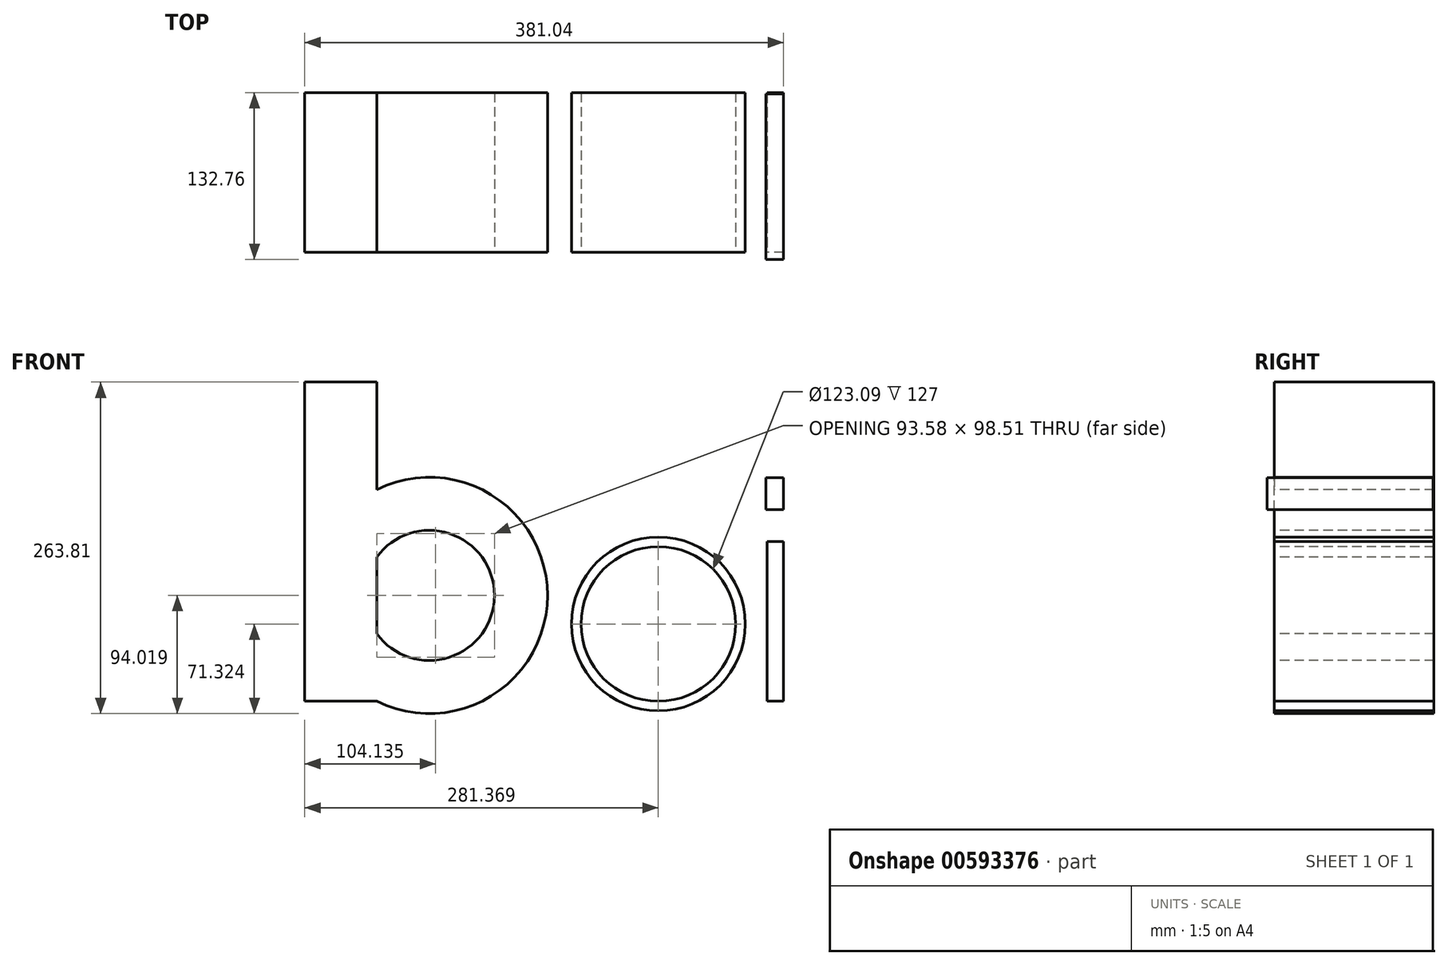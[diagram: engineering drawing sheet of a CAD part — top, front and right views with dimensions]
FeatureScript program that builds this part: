
annotation { "Feature Type Name" : "Feature", "Feature Type Description" : "" }
export const myFeature = defineFeature(function(context is Context, id is Id, definition is map)
    precondition{}
    {
        {
            var Q0;
            Q0=qCreatedBy(makeId("Top.planeOp"),FACE);
            var sketch = newSketch(context, id + "F0", { "sketchPlane" : qUnion([Q0])});
            skLineSegment(sketch, "E0.bottom", {"start": v(190.5, 63.5) * mm, "end": v(-190.5, 63.5) * mm});
            skLineSegment(sketch, "E0.top", {"start": v(190.5, -63.5) * mm, "end": v(-190.5, -63.5) * mm});
            skLineSegment(sketch, "E0.left", {"start": v(190.5, 63.5) * mm, "end": v(190.5, -63.5) * mm});
            skLineSegment(sketch, "E0.right", {"start": v(-190.5, 63.5) * mm, "end": v(-190.5, -63.5) * mm});
            skPoint(sketch, "E0.middle", {"position": v(0, 0) * mm});
            skLineSegment(sketch, "E1", {"start": v(-133.15, -63.5) * mm, "end": v(-133.15, 63.5) * mm});
            skLineSegment(sketch, "E2", {"start": v(-38.93, 63.5) * mm, "end": v(-38.93, -63.5) * mm});
            skLineSegment(sketch, "E3", {"start": v(59.74, 63.5) * mm, "end": v(59.74, -63.5) * mm});
            skLineSegment(sketch, "E4", {"start": v(59.74, -63.5) * mm, "end": v(122.52, -63.5) * mm});
            skLineSegment(sketch, "E5", {"start": v(122.52, 63.5) * mm, "end": v(122.52, -63.5) * mm});
            skLineSegment(sketch, "E6", {"start": v(88.9, 63.5) * mm, "end": v(88.9, -63.5) * mm});
            skLineSegment(sketch, "E7", {"start": v(177.27, 63.5) * mm, "end": v(177.27, -63.5) * mm});
            skSolve(sketch);
        }
        {
            var Q0;
            {var subQ0=sQuery(id+"F0.wireOp",EDGE,"E0.right");Q0=makeQuery(id+"F0.imprint","IMPRINT",FACE,{"disambiguationData":[TD([[makeQuery(id+"F0.imprint","IMPRINT",EDGE,{"derivedFrom":subQ0}),1.0]])]});}
            extrude(context, id + "F1", {"entities" : qUnion([Q0]), "depth" : 254 * mm, "offsetDistance" : 25.4 * mm});
        }
        {
            var Q0;
            Q0=qCreatedBy(makeId("Front.planeOp"),FACE);
            var sketch = newSketch(context, id + "F2", { "sketchPlane" : qUnion([Q0])});
            skCircle(sketch, "E8", {"center": v(-91.34, 84.2) * mm, "radius": 37.73 * mm});
            skSolve(sketch);
        }
        {
            var Q0;
            Q0=makeQuery(id+"F1.opExtrude","SWEPT_FACE",FACE,{"disambiguationData":[OSD([sQuery(id+"F0.wireOp",EDGE,"E1")])]});
            var sketch = newSketch(context, id + "F3", { "sketchPlane" : qUnion([Q0])});
            skLineSegment(sketch, "E9", {"start": v(-63.5, 53.7) * mm, "end": v(63.5, 53.7) * mm});
            skSolve(sketch);
        }
        {
            var Q0;
            {var subQ0=sQuery(id+"F3.wireOp",EDGE,"E9");Q0=makeQuery(id+"F3.imprint","IMPRINT",FACE,{"disambiguationData":[TD([[makeQuery(id+"F3.imprint","IMPRINT",EDGE,{"derivedFrom":subQ0}),-1.0]])]});}
            var Q1;
            Q1=sQuery(id+"F2.wireOp",EDGE,"E8");
            sweep(context, id + "F4", {"operationType" : NewBodyOperationType.ADD, "profiles" : qUnion([Q0]), "path" : qUnion([Q1])});
        }
        {
            var Q0;
            {var subQ0=sQuery(id+"F0.wireOp",EDGE,"E3");Q0=makeQuery(id+"F0.imprint","IMPRINT",FACE,{"disambiguationData":[TD([[makeQuery(id+"F0.imprint","IMPRINT",EDGE,{"derivedFrom":subQ0}),1.0]])]});}
            cPlane(context, id + "F5", {"entities" : qUnion([Q0]), "cplaneType" : CPlaneType.OFFSET, "offset" : 127 * mm, "width" : 152.4 * mm, "height" : 152.4 * mm});
        }
        {
            var Q0;
            Q0=qCreatedBy(makeId("Front.planeOp"),FACE);
            var sketch = newSketch(context, id + "F6", { "sketchPlane" : qUnion([Q0])});
            skCircle(sketch, "E10", {"center": v(90.87, 61.51) * mm, "radius": 66.84 * mm});
            skSolve(sketch);
        }
        {
            var Q0;
            {var subQ0=sQuery(id+"F0.wireOp",EDGE,"E5");Q0=makeQuery(id+"F0.imprint","IMPRINT",FACE,{"disambiguationData":[TD([[makeQuery(id+"F0.imprint","IMPRINT",EDGE,{"derivedFrom":subQ0}),-1.0]])]});}
            var Q1;
            Q1=sQuery(id+"F6.wireOp",EDGE,"E10");
            sweep(context, id + "F7", {"profiles" : qUnion([Q0]), "path" : qUnion([Q1])});
        }
        {
            var Q0;
            {var subQ0=sQuery(id+"F0.wireOp",EDGE,"E0.left");Q0=makeQuery(id+"F0.imprint","IMPRINT",FACE,{"disambiguationData":[TD([[makeQuery(id+"F0.imprint","IMPRINT",EDGE,{"derivedFrom":subQ0}),-1.0]])]});}
            extrude(context, id + "F8", {"entities" : qUnion([Q0]), "depth" : 127 * mm, "offsetDistance" : 25.4 * mm});
        }
        {
            var Q0;
            Q0=makeQuery(id+"F8.opExtrude","CAP_FACE",FACE,{"disambiguationData":[OSD([sQuery(id+"F0.wireOp",EDGE,"E0.bottom"),sQuery(id+"F0.wireOp",EDGE,"E0.top"),sQuery(id+"F0.wireOp",EDGE,"E0.left"),sQuery(id+"F0.wireOp",EDGE,"E7")])],"isStart":false});
            cPlane(context, id + "F9", {"entities" : qUnion([Q0]), "cplaneType" : CPlaneType.OFFSET, "offset" : 25.4 * mm, "width" : 152.4 * mm, "height" : 152.4 * mm});
        }
        {
            var Q0;
            Q0=qCreatedBy(id+"F9.planeOp",FACE);
            var sketch = newSketch(context, id + "F10", { "sketchPlane" : qUnion([Q0])});
            skLineSegment(sketch, "E11.bottom", {"start": v(190.54, 62.7) * mm, "end": v(176.55, 62.7) * mm});
            skLineSegment(sketch, "E11.top", {"start": v(190.54, -69.26) * mm, "end": v(176.55, -69.26) * mm});
            skLineSegment(sketch, "E11.left", {"start": v(190.54, 62.7) * mm, "end": v(190.54, -69.26) * mm});
            skLineSegment(sketch, "E11.right", {"start": v(176.55, 62.7) * mm, "end": v(176.55, -69.26) * mm});
            skPoint(sketch, "E11.middle", {"position": v(183.55, -3.28) * mm});
            skSolve(sketch);
        }
        {
            var Q0;
            Q0=makeQuery(id+"F10.imprint","IMPRINT",FACE,{"disambiguationData":[TD([[makeQuery(id+"F10.imprint","IMPRINT",EDGE,{"derivedFrom":sQuery(id+"F10.wireOp",EDGE,"E11.bottom")}),1.0]])]});
            extrude(context, id + "F11", {"entities" : qUnion([Q0]), "depth" : 25.4 * mm, "offsetDistance" : 25.4 * mm});
        }
    });
